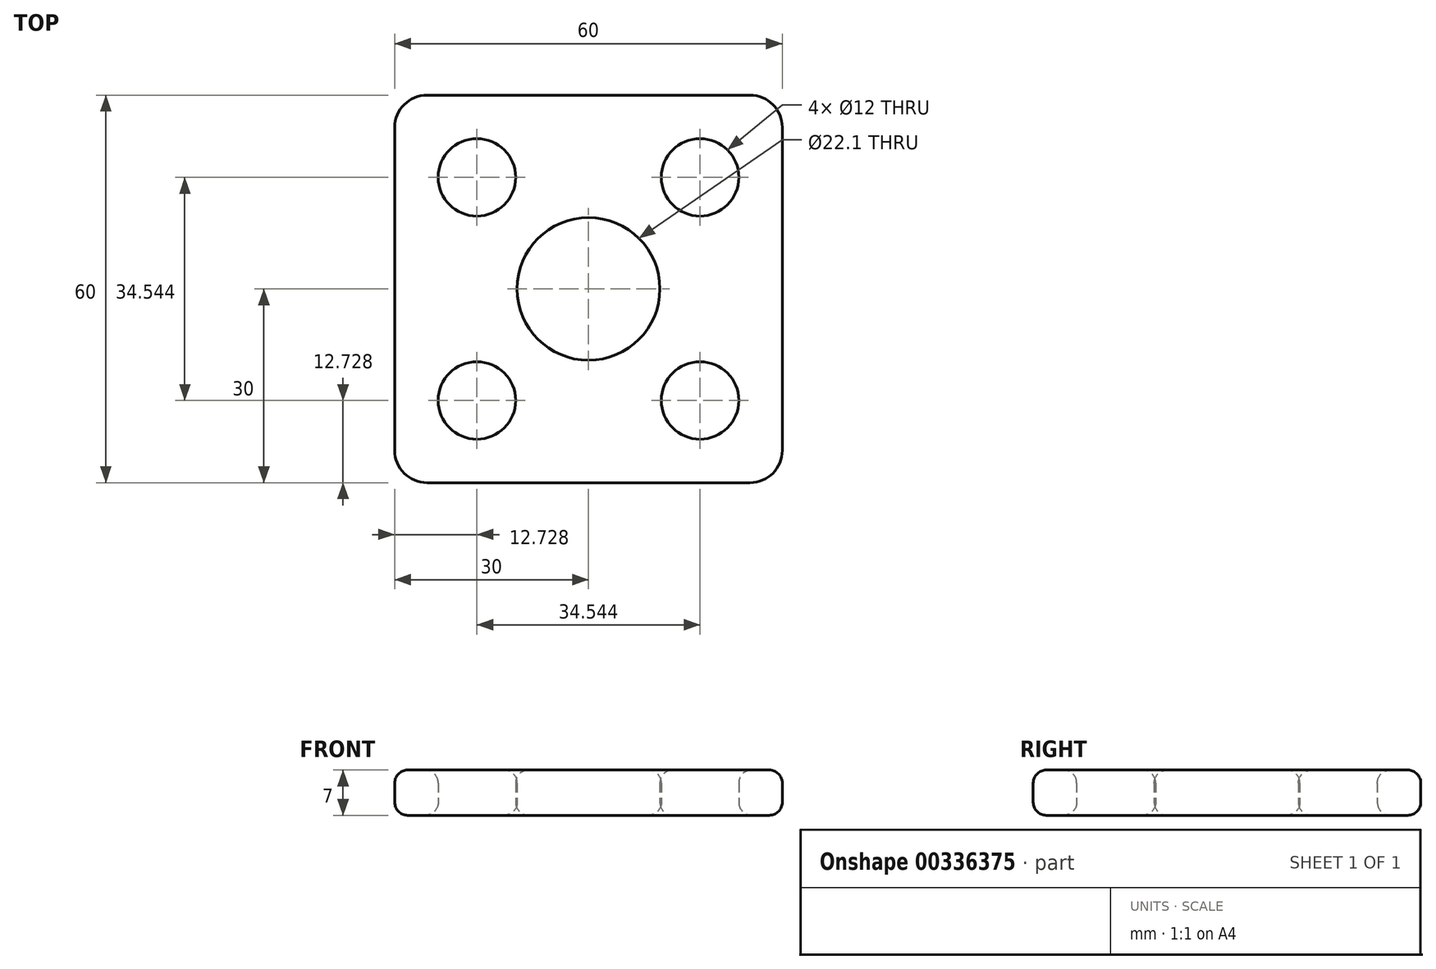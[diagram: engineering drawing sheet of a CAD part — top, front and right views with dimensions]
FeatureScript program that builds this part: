
annotation { "Feature Type Name" : "Feature", "Feature Type Description" : "" }
export const myFeature = defineFeature(function(context is Context, id is Id, definition is map)
    precondition{}
    {
        {
            var Q0;
            Q0=qCreatedBy(makeId("Top.planeOp"),FACE);
            var sketch = newSketch(context, id + "F0", { "sketchPlane" : qUnion([Q0])});
            skLineSegment(sketch, "E0.bottom", {"start": v(30, 30) * mm, "end": v(-30, 30) * mm});
            skLineSegment(sketch, "E0.top", {"start": v(30, -30) * mm, "end": v(-30, -30) * mm});
            skLineSegment(sketch, "E0.left", {"start": v(30, 30) * mm, "end": v(30, -30) * mm});
            skLineSegment(sketch, "E0.right", {"start": v(-30, 30) * mm, "end": v(-30, -30) * mm});
            skPoint(sketch, "E0.middle", {"position": v(0, 0) * mm});
            skCircle(sketch, "E1", {"center": v(0, 0) * mm, "radius": 11.05 * mm});
            skLineSegment(sketch, "E2", {"start": v(-30, 30) * mm, "end": v(0, 0) * mm});
            skCircle(sketch, "E3", {"center": v(-17.27, 17.27) * mm, "radius": 6 * mm});
            skCircle(sketch, "E4.MirrorC", {"center": v(17.27, 17.27) * mm, "radius": 6 * mm});
            skCircle(sketch, "E5.MirrorC", {"center": v(17.27, -17.27) * mm, "radius": 6 * mm});
            skCircle(sketch, "E6.MirrorC", {"center": v(-17.27, -17.27) * mm, "radius": 6 * mm});
            skSolve(sketch);
        }
        {
            var Q0;
            Q0=makeQuery(id+"F0.imprint","IMPRINT",FACE,{"disambiguationData":[TD([[makeQuery(id+"F0.imprint","IMPRINT",EDGE,{"derivedFrom":sQuery(id+"F0.wireOp",EDGE,"E0.bottom")}),1.0]])]});
            extrude(context, id + "F1", {"entities" : qUnion([Q0]), "depth" : 7 * mm, "offsetDistance" : 25 * mm});
        }
        {
            var Q0;
            Q0=makeQuery(id+"F1.opExtrude","CAP_FACE",FACE,{"disambiguationData":[OSD([sQuery(id+"F0.wireOp",EDGE,"E0.bottom"),sQuery(id+"F0.wireOp",EDGE,"E0.top"),sQuery(id+"F0.wireOp",EDGE,"E0.left"),sQuery(id+"F0.wireOp",EDGE,"E0.right"),sQuery(id+"F0.wireOp",EDGE,"E1"),sQuery(id+"F0.wireOp",EDGE,"E3"),sQuery(id+"F0.wireOp",EDGE,"E4.MirrorC"),sQuery(id+"F0.wireOp",EDGE,"E5.MirrorC"),sQuery(id+"F0.wireOp",EDGE,"E6.MirrorC")])],"isStart":false});
            var Q1;
            Q1=makeQuery(id+"F1.opExtrude","CAP_FACE",FACE,{"disambiguationData":[OSD([sQuery(id+"F0.wireOp",EDGE,"E0.bottom"),sQuery(id+"F0.wireOp",EDGE,"E0.top"),sQuery(id+"F0.wireOp",EDGE,"E0.left"),sQuery(id+"F0.wireOp",EDGE,"E0.right"),sQuery(id+"F0.wireOp",EDGE,"E1"),sQuery(id+"F0.wireOp",EDGE,"E3"),sQuery(id+"F0.wireOp",EDGE,"E4.MirrorC"),sQuery(id+"F0.wireOp",EDGE,"E5.MirrorC"),sQuery(id+"F0.wireOp",EDGE,"E6.MirrorC")])],"isStart":true});
            fillet(context, id + "F2", {"entities" : qUnion([Q0, Q1]), "tangentPropagation" : true, "radius" : 2 * mm, "defaultsChanged" : true, "vertexSettings" : [], "allowEdgeOverflow" : false});
        }
        {
            var Q0;
            Q0=makeQuery(id+"F1.opExtrude","SWEPT_EDGE",EDGE,{"disambiguationData":[OSD([sQuery(id+"F0.wireOp",EDGE,"E0.top"),sQuery(id+"F0.wireOp",EDGE,"E0.right")])]});
            var Q1;
            Q1=makeQuery(id+"F1.opExtrude","SWEPT_EDGE",EDGE,{"disambiguationData":[OSD([sQuery(id+"F0.wireOp",EDGE,"E0.bottom"),sQuery(id+"F0.wireOp",EDGE,"E0.right")])]});
            var Q2;
            Q2=makeQuery(id+"F1.opExtrude","SWEPT_EDGE",EDGE,{"disambiguationData":[OSD([sQuery(id+"F0.wireOp",EDGE,"E0.bottom"),sQuery(id+"F0.wireOp",EDGE,"E0.left")])]});
            var Q3;
            Q3=makeQuery(id+"F1.opExtrude","SWEPT_EDGE",EDGE,{"disambiguationData":[OSD([sQuery(id+"F0.wireOp",EDGE,"E0.top"),sQuery(id+"F0.wireOp",EDGE,"E0.left")])]});
            fillet(context, id + "F3", {"entities" : qUnion([Q0, Q1, Q2, Q3]), "tangentPropagation" : true, "radius" : 5 * mm, "defaultsChanged" : false, "vertexSettings" : [], "allowEdgeOverflow" : false});
        }
    });
